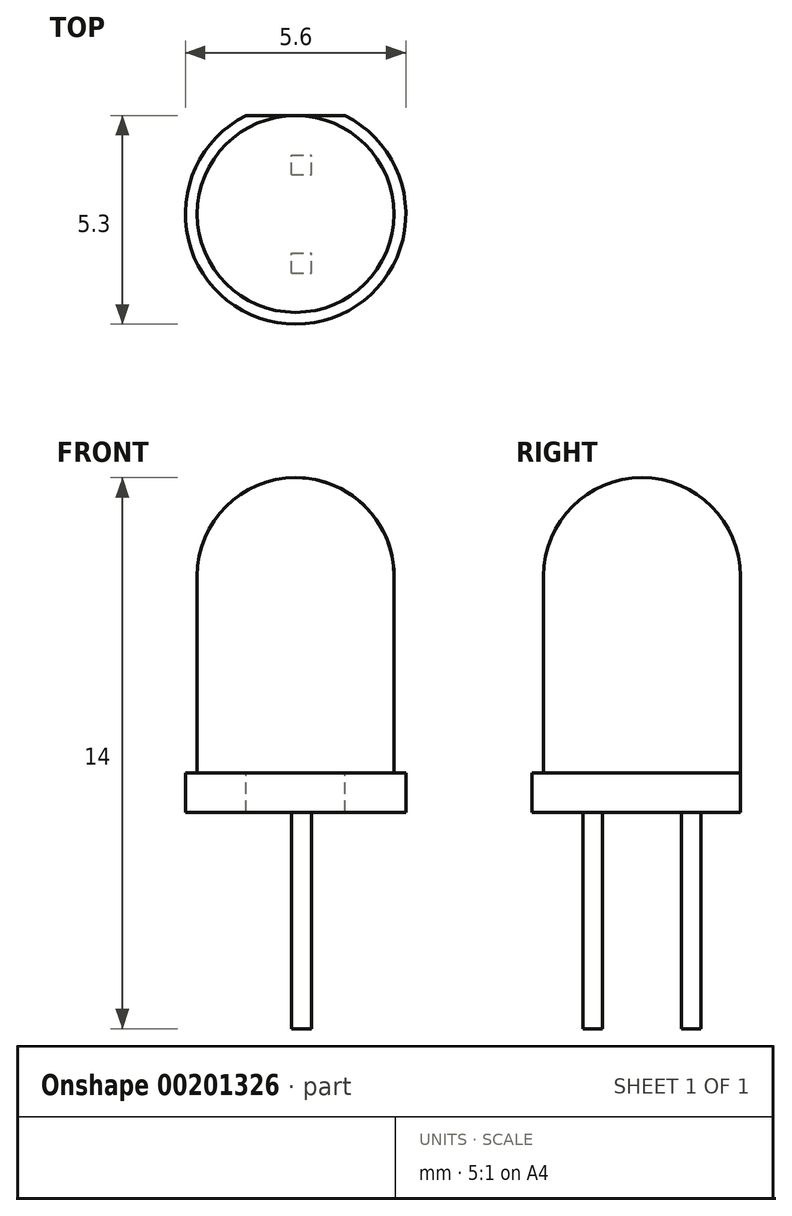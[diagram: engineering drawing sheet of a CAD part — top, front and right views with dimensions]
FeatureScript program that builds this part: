
annotation { "Feature Type Name" : "Feature", "Feature Type Description" : "" }
export const myFeature = defineFeature(function(context is Context, id is Id, definition is map)
    precondition{}
    {
        {
            var Q0;
            Q0=qCreatedBy(makeId("Top.planeOp"),FACE);
            var sketch = newSketch(context, id + "F0", { "sketchPlane" : qUnion([Q0])});
            skCircle(sketch, "E0", {"center": v(0, 0) * mm, "radius": 2.5 * mm});
            skSolve(sketch);
        }
        {
            var Q0;
            Q0=makeQuery(id+"F0.imprint","IMPRINT",FACE,{"disambiguationData":[TD([[makeQuery(id+"F0.imprint","IMPRINT",EDGE,{"derivedFrom":sQuery(id+"F0.wireOp",EDGE,"E0")}),1.0]])]});
            extrude(context, id + "F1", {"entities" : qUnion([Q0]), "depth" : 7.5 * mm});
        }
        {
            var Q0;
            Q0=makeQuery(id+"F1.opExtrude","CAP_EDGE",EDGE,{"disambiguationData":[OSD([sQuery(id+"F0.wireOp",EDGE,"E0")])],"isStart":false});
            fillet(context, id + "F2", {"entities" : qUnion([Q0]), "radius" : 2.5 * mm, "tangentPropagation" : true, "allowEdgeOverflow" : false});
        }
        {
            var Q0;
            Q0=makeQuery(id+"F1.opExtrude","CAP_FACE",FACE,{"disambiguationData":[OSD([sQuery(id+"F0.wireOp",EDGE,"E0")])],"isStart":true});
            var sketch = newSketch(context, id + "F3", { "sketchPlane" : qUnion([Q0])});
            skArc(sketch, "E1", {"start": v(1.26, -2.5) * mm, "mid": v(0, 2.8) * mm, "end": v(-1.26, -2.5) * mm});
            skLineSegment(sketch, "E2", {"start": v(-1.26, -2.5) * mm, "end": v(1.26, -2.5) * mm});
            skSolve(sketch);
        }
        {
            var Q0;
            Q0 = qSketchRegion(id + "F3", true);
            extrude(context, id + "F4", {"entities" : qUnion([Q0]), "operationType" : NewBodyOperationType.ADD, "depth" : 1 * mm});
        }
        {
            var Q0;
            Q0=makeQuery(id+"F4.opExtrude","CAP_FACE",FACE,{"disambiguationData":[OSD([sQuery(id+"F3.wireOp",EDGE,"E1")])],"isStart":false});
            cPlane(context, id + "F5", {"entities" : qUnion([Q0]), "cplaneType" : CPlaneType.OFFSET, "offset" : 0 * mm, "width" : 150 * mm, "height" : 150 * mm});
        }
        {
            var Q0;
            Q0=qCreatedBy(id+"F5.planeOp",FACE);
            var sketch = newSketch(context, id + "F6", { "sketchPlane" : qUnion([Q0])});
            skLineSegment(sketch, "E3", {"start": v(0.15, 2.8) * mm, "end": v(0.15, -2.8) * mm, "construction": true});
            skLineSegment(sketch, "E4", {"start": v(2.95, 0) * mm, "end": v(-2.35, 0) * mm, "construction": true});
            skLineSegment(sketch, "E5.bottom", {"start": v(-0.1, 1.5) * mm, "end": v(0.4, 1.5) * mm});
            skLineSegment(sketch, "E5.top", {"start": v(-0.1, 1) * mm, "end": v(0.4, 1) * mm});
            skLineSegment(sketch, "E5.left", {"start": v(-0.1, 1.5) * mm, "end": v(-0.1, 1) * mm});
            skLineSegment(sketch, "E5.right", {"start": v(0.4, 1.5) * mm, "end": v(0.4, 1) * mm});
            skLineSegment(sketch, "E6.bottom", {"start": v(-0.1, -1) * mm, "end": v(0.4, -1) * mm});
            skLineSegment(sketch, "E6.top", {"start": v(-0.1, -1.5) * mm, "end": v(0.4, -1.5) * mm});
            skLineSegment(sketch, "E6.left", {"start": v(-0.1, -1) * mm, "end": v(-0.1, -1.5) * mm});
            skLineSegment(sketch, "E6.right", {"start": v(0.4, -1) * mm, "end": v(0.4, -1.5) * mm});
            skSolve(sketch);
        }
        {
            var Q0;
            Q0 = qSketchRegion(id + "F6", true);
            extrude(context, id + "F7", {"entities" : qUnion([Q0]), "operationType" : NewBodyOperationType.ADD, "depth" : 5.5 * mm});
        }
    });
